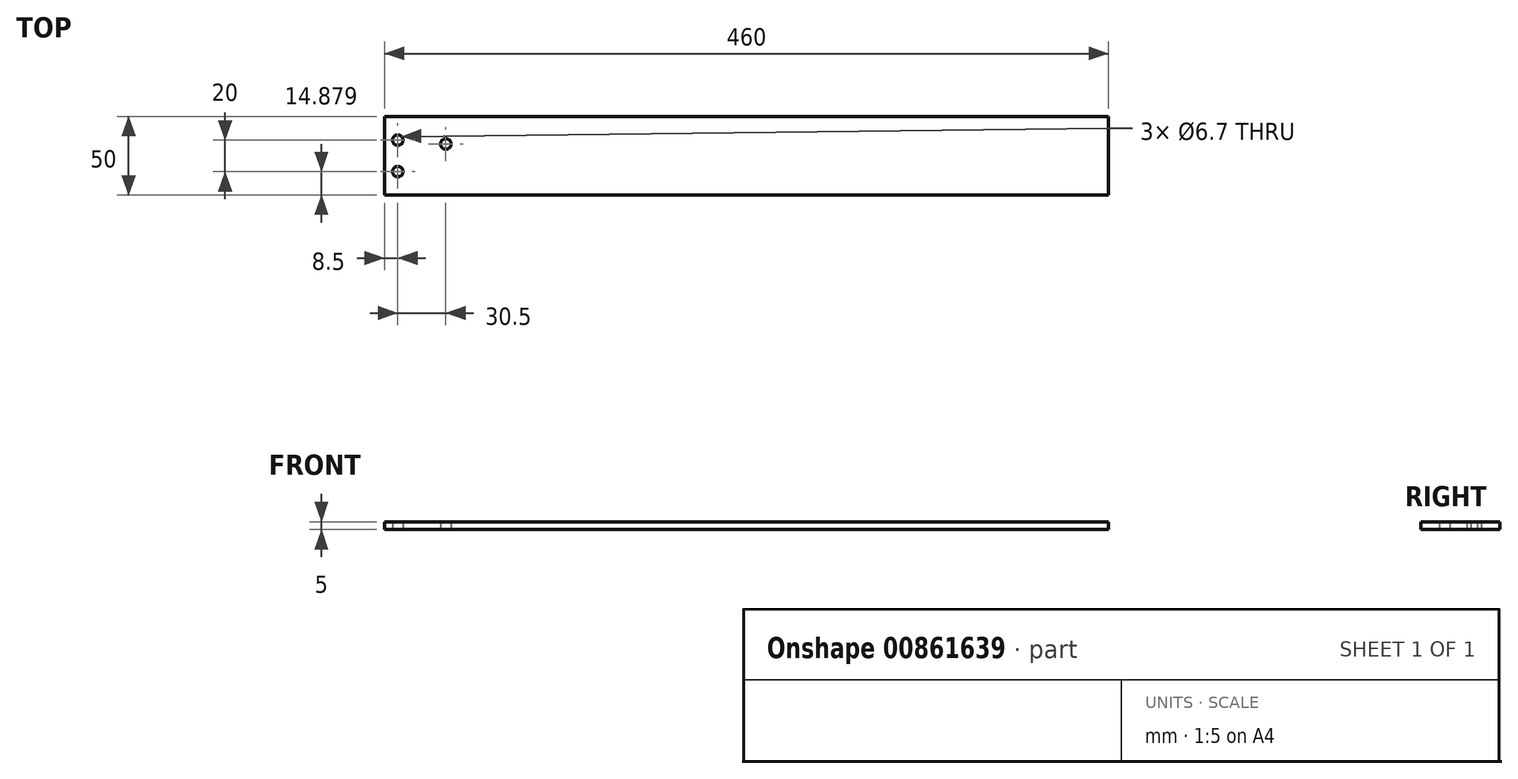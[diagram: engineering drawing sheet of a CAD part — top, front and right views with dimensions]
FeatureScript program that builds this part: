
annotation { "Feature Type Name" : "Feature", "Feature Type Description" : "" }
export const myFeature = defineFeature(function(context is Context, id is Id, definition is map)
    precondition{}
    {
        {
            var Q0;
            Q0=qCreatedBy(makeId("Top.planeOp"),FACE);
            var sketch = newSketch(context, id + "F0", { "sketchPlane" : qUnion([Q0])});
            skLineSegment(sketch, "E0.bottom", {"start": v(-230, 25) * mm, "end": v(230, 25) * mm});
            skLineSegment(sketch, "E0.top", {"start": v(-230, -25) * mm, "end": v(230, -25) * mm});
            skLineSegment(sketch, "E0.left", {"start": v(-230, 25) * mm, "end": v(-230, -25) * mm});
            skLineSegment(sketch, "E0.right", {"start": v(230, 25) * mm, "end": v(230, -25) * mm});
            skPoint(sketch, "E0.middle", {"position": v(0, 0) * mm});
            skCircle(sketch, "E1", {"center": v(-221.5, 9.88) * mm, "radius": 3.35 * mm});
            skCircle(sketch, "E2", {"center": v(-221.5, -10.12) * mm, "radius": 3.35 * mm});
            skCircle(sketch, "E3", {"center": v(-191, 7.4) * mm, "radius": 3.35 * mm});
            skSolve(sketch);
        }
        {
            var Q0;
            Q0 = qSketchRegion(id + "F0", true);
            extrude(context, id + "F1", {"entities" : qUnion([Q0]), "depth" : 5 * mm, "offsetDistance" : 25 * mm});
        }
    });
